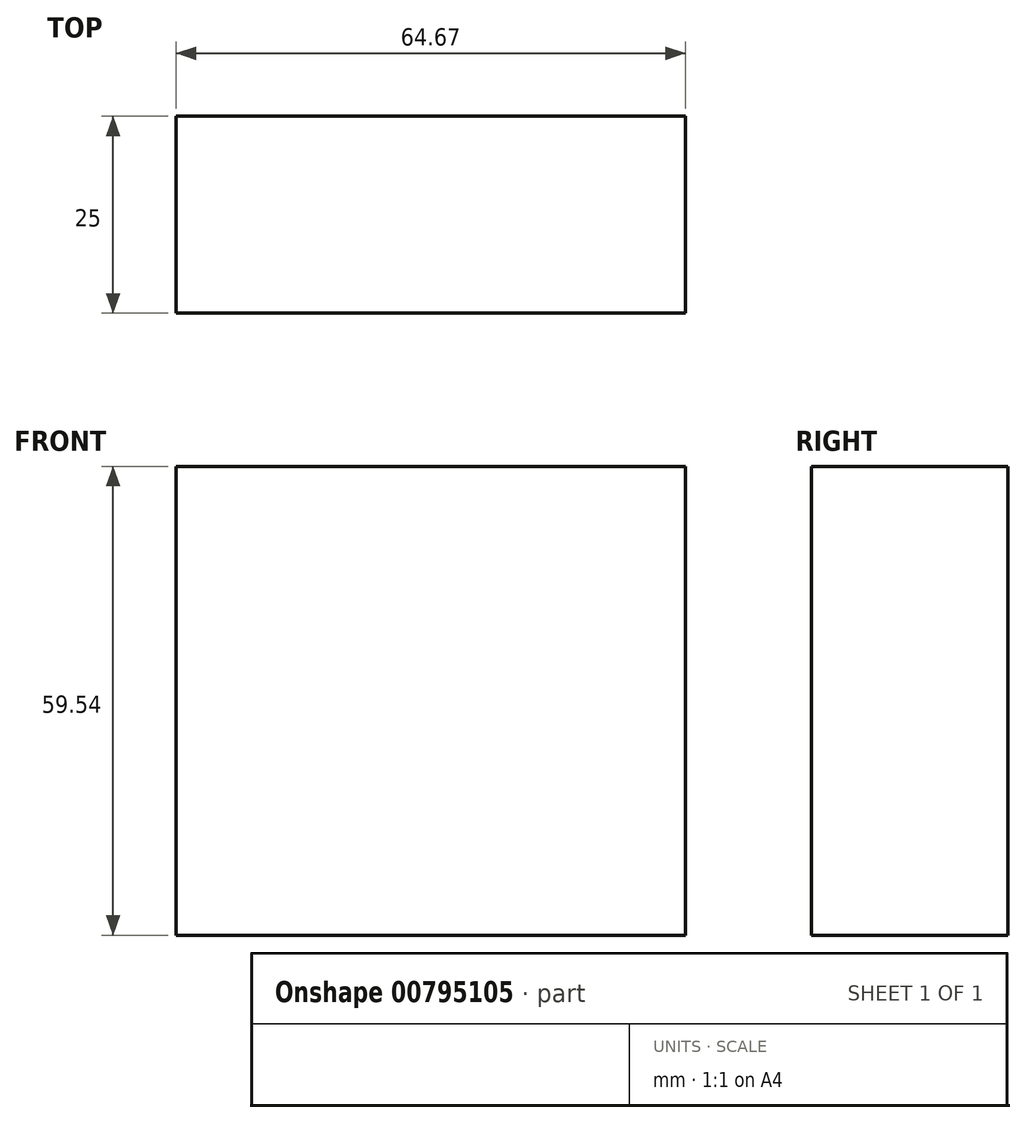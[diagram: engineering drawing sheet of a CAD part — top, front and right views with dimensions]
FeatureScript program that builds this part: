
annotation { "Feature Type Name" : "Feature", "Feature Type Description" : "" }
export const myFeature = defineFeature(function(context is Context, id is Id, definition is map)
    precondition{}
    {
        {
            var Q0;
            Q0=qCreatedBy(makeId("Front.planeOp"),FACE);
            var sketch = newSketch(context, id + "F0", { "sketchPlane" : qUnion([Q0])});
            skLineSegment(sketch, "E0.bottom", {"start": v(0, 0) * mm, "end": v(64.67, 0) * mm});
            skLineSegment(sketch, "E0.top", {"start": v(0, 59.54) * mm, "end": v(64.67, 59.54) * mm});
            skLineSegment(sketch, "E0.left", {"start": v(0, 0) * mm, "end": v(0, 59.54) * mm});
            skLineSegment(sketch, "E0.right", {"start": v(64.67, 0) * mm, "end": v(64.67, 59.54) * mm});
            skSolve(sketch);
        }
        {
            var Q0;
            Q0=makeQuery(id+"F0.imprint","IMPRINT",FACE,{"disambiguationData":[TD([[makeQuery(id+"F0.imprint","IMPRINT",EDGE,{"derivedFrom":sQuery(id+"F0.wireOp",EDGE,"E0.bottom")}),1.0]])]});
            var sketch = newSketch(context, id + "F1", { "sketchPlane" : qUnion([Q0])});
            skSolve(sketch);
        }
        {
            var Q0;
            Q0=makeQuery(id+"F1.imprint","IMPRINT",FACE,{"disambiguationData":[TD([[makeQuery(id+"F1.imprint","IMPRINT",EDGE,{"derivedFrom":makeQuery(id+"F0.imprint","IMPRINT",EDGE,{"derivedFrom":sQuery(id+"F0.wireOp",EDGE,"E0.bottom")})}),1.0]])]});
            extrude(context, id + "F2", {"entities" : qUnion([Q0]), "depth" : 25 * mm, "offsetDistance" : 25 * mm});
        }
    });
